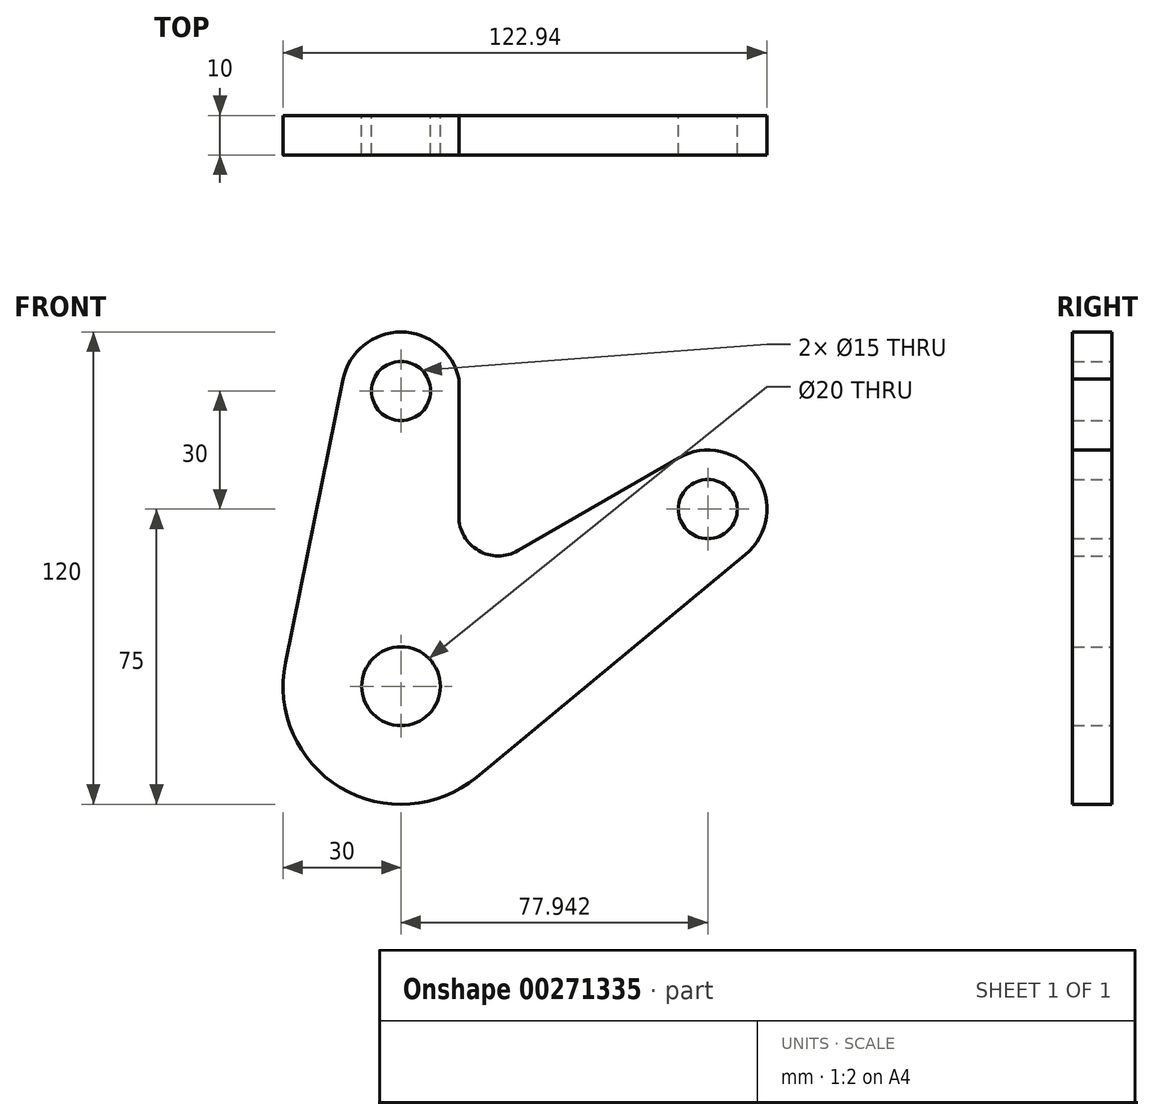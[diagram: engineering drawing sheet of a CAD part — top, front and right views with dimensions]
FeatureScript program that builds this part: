
annotation { "Feature Type Name" : "Feature", "Feature Type Description" : "" }
export const myFeature = defineFeature(function(context is Context, id is Id, definition is map)
    precondition{}
    {
        {
            var Q0;
            Q0=qCreatedBy(makeId("Front.planeOp"),FACE);
            var sketch = newSketch(context, id + "F0", { "sketchPlane" : qUnion([Q0])});
            skCircle(sketch, "E0", {"center": v(0, 0) * mm, "radius": 10 * mm});
            skCircle(sketch, "E1", {"center": v(0, 75) * mm, "radius": 7.5 * mm});
            skArc(sketch, "E2", {"start": v(-29.4, 6) * mm, "mid": v(-15.44, -25.72) * mm, "end": v(19.12, -23.12) * mm});
            skLineSegment(sketch, "E3", {"start": v(-29.4, 6) * mm, "end": v(-14.7, 78) * mm});
            skLineSegment(sketch, "E4", {"start": v(19.12, -23.12) * mm, "end": v(87.5, 33.44) * mm});
            skCircle(sketch, "E5", {"center": v(77.94, 45) * mm, "radius": 7.5 * mm});
            skLineSegment(sketch, "E6", {"start": v(0, 75) * mm, "end": v(0, 0) * mm, "construction": true});
            skLineSegment(sketch, "E7", {"start": v(0, 0) * mm, "end": v(77.94, 45) * mm, "construction": true});
            skArc(sketch, "E8", {"start": v(14.7, 78) * mm, "mid": v(0, 90) * mm, "end": v(-14.7, 78) * mm});
            skArc(sketch, "E9", {"start": v(87.5, 33.44) * mm, "mid": v(90.26, 53.56) * mm, "end": v(70.44, 58) * mm});
            skLineSegment(sketch, "E10", {"start": v(14.7, 78) * mm, "end": v(14.7, 43.13) * mm});
            skLineSegment(sketch, "E11", {"start": v(70.44, 58) * mm, "end": v(29.7, 34.47) * mm});
            skArc(sketch, "E12", {"start": v(14.7, 43.13) * mm, "mid": v(19.7, 34.47) * mm, "end": v(29.7, 34.47) * mm});
            skSolve(sketch);
        }
        {
            var Q0;
            Q0=makeQuery(id+"F0.imprint","IMPRINT",FACE,{"disambiguationData":[TD([[makeQuery(id+"F0.imprint","IMPRINT",EDGE,{"derivedFrom":sQuery(id+"F0.wireOp",EDGE,"E0")}),-1.0]])]});
            extrude(context, id + "F1", {"entities" : qUnion([Q0]), "depth" : 10 * mm});
        }
    });
